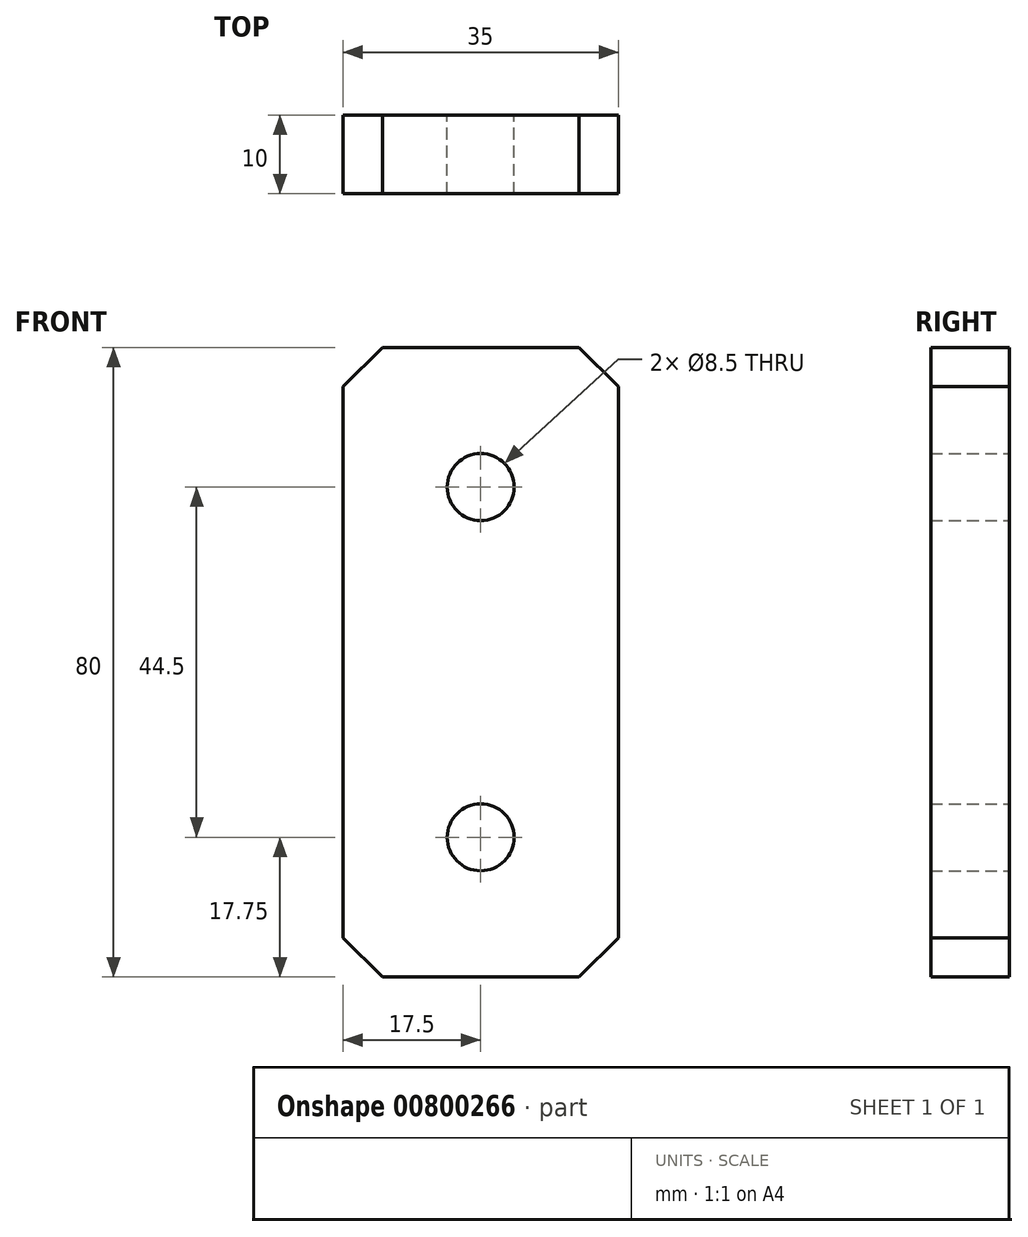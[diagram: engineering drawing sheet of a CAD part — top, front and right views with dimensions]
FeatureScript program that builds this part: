
annotation { "Feature Type Name" : "Feature", "Feature Type Description" : "" }
export const myFeature = defineFeature(function(context is Context, id is Id, definition is map)
    precondition{}
    {
        {
            var Q0;
            Q0=qCreatedBy(makeId("Front.planeOp"),FACE);
            var sketch = newSketch(context, id + "F0", { "sketchPlane" : qUnion([Q0])});
            skLineSegment(sketch, "E0.bottom", {"start": v(-17.5, 40) * mm, "end": v(17.5, 40) * mm});
            skLineSegment(sketch, "E0.top", {"start": v(-17.5, -40) * mm, "end": v(17.5, -40) * mm});
            skLineSegment(sketch, "E0.left", {"start": v(-17.5, 40) * mm, "end": v(-17.5, -40) * mm});
            skLineSegment(sketch, "E0.right", {"start": v(17.5, 40) * mm, "end": v(17.5, -40) * mm});
            skPoint(sketch, "E0.middle", {"position": v(0, 0) * mm});
            skLineSegment(sketch, "E1", {"start": v(0, 40) * mm, "end": v(0, -40) * mm, "construction": true});
            skCircle(sketch, "E2", {"center": v(0, 22.25) * mm, "radius": 4.25 * mm});
            skCircle(sketch, "E3", {"center": v(0, -22.25) * mm, "radius": 4.25 * mm});
            skLineSegment(sketch, "E4", {"start": v(-17.5, 0) * mm, "end": v(17.5, 0) * mm, "construction": true});
            skSolve(sketch);
        }
        {
            var Q0;
            Q0 = qSketchRegion(id + "F0", true);
            extrude(context, id + "F1", {"entities" : qUnion([Q0]), "depth" : 10 * mm, "offsetDistance" : 25 * mm});
        }
        {
            var Q0;
            Q0=makeQuery(id+"F1.opExtrude","SWEPT_EDGE",EDGE,{"disambiguationData":[OSD([sQuery(id+"F0.wireOp",EDGE,"E0.bottom"),sQuery(id+"F0.wireOp",EDGE,"E0.left")])]});
            var Q1;
            Q1=makeQuery(id+"F1.opExtrude","SWEPT_EDGE",EDGE,{"disambiguationData":[OSD([sQuery(id+"F0.wireOp",EDGE,"E0.bottom"),sQuery(id+"F0.wireOp",EDGE,"E0.right")])]});
            var Q2;
            Q2=makeQuery(id+"F1.opExtrude","SWEPT_EDGE",EDGE,{"disambiguationData":[OSD([sQuery(id+"F0.wireOp",EDGE,"E0.top"),sQuery(id+"F0.wireOp",EDGE,"E0.left")])]});
            var Q3;
            Q3=makeQuery(id+"F1.opExtrude","SWEPT_EDGE",EDGE,{"disambiguationData":[OSD([sQuery(id+"F0.wireOp",EDGE,"E0.top"),sQuery(id+"F0.wireOp",EDGE,"E0.right")])]});
            chamfer(context, id + "F2", {"entities" : qUnion([Q0, Q1, Q2, Q3]), "width" : 5 * mm, "tangentPropagation" : true});
        }
    });
